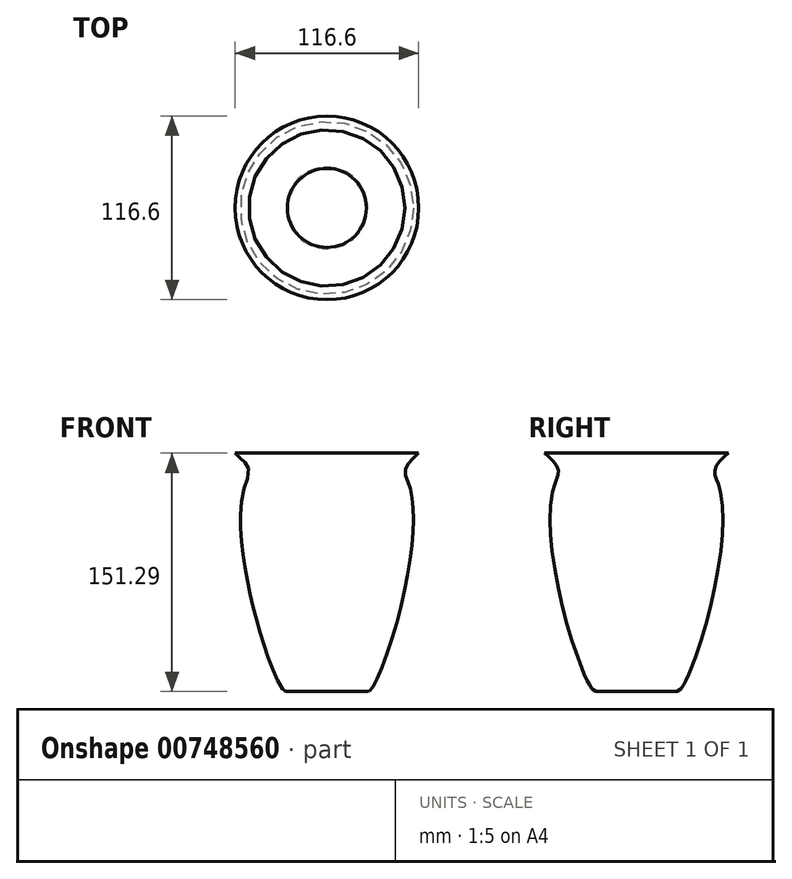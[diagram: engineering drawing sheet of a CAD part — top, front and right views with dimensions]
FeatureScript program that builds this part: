
annotation { "Feature Type Name" : "Feature", "Feature Type Description" : "" }
export const myFeature = defineFeature(function(context is Context, id is Id, definition is map)
    precondition{}
    {
        {
            var Q0;
            Q0=qCreatedBy(makeId("Front.planeOp"),FACE);
            var sketch = newSketch(context, id + "F0", { "sketchPlane" : qUnion([Q0])});
            skFitSpline(sketch, "E0", {"points": [v(-58.3, 76.34) * mm, v(-49.79, 65.97) * mm, v(-52.49, 54.98) * mm, v(-54.56, 24.9) * mm, v(-42.53, -37.55) * mm, v(-27.38, -74.27) * mm, v(-25.1, -74.9) * mm], "startDerivative": vector(90.19, -79.55) * mm, "endDerivative": vector(38.9, 3.34) * mm});
            skLineSegment(sketch, "E1", {"start": v(-25.8, -74.95) * mm, "end": v(0, -74.95) * mm});
            skLineSegment(sketch, "E2", {"start": v(0, -74.95) * mm, "end": v(0, 76.34) * mm});
            skSolve(sketch);
        }
        {
            var Q0;
            Q0=sQuery(id+"F0.wireOp",EDGE,"E0");
            var Q1;
            Q1=sQuery(id+"F0.wireOp",EDGE,"E1");
            var Q2;
            Q2=sQuery(id+"F0.wireOp",EDGE,"E2");
            revolve(context, id + "F1", {"bodyType" : ToolBodyType.SURFACE, "surfaceOperationType" : NewSurfaceOperationType.NEW, "surfaceEntities" : qUnion([Q0, Q1]), "axis" : qUnion([Q2]), "revolveType" : RevolveType.FULL});
        }
    });
